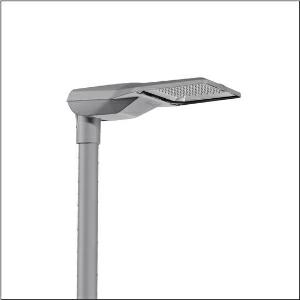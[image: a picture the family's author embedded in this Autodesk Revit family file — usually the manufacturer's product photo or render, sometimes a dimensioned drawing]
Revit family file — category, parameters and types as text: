
# Revit family: streetlight_sl_21_iq_midi___st0_8a_5xe3c31d08nb_f3e6
name_source: partatom
category: Lighting Fixtures
units: mm (PartAtom-declared; Revit-internal decimal feet)

## family parameters
Cut with Voids When Loaded = No
Host = Face
Light Source = No
Part Type = Normal
Room Calculation Point = No
Round Connector Dimension = Use Diameter
Shared = No

## types (1)
- --- (1 x LED, 23230 lm, 155.5 W, 3000K)
    Apparent Load = 155 VA
    CIE Flux Codes = 41 75 97 100 100
    Color Rendering = 70
    Color Temperature = 3000K
    Default Elevation = 1800 mm
    Description = Streetlight SL 21 iQ midi, mast luminaire, primary light control with lens, of PMMA, primary optical cover: cover, of toughened safety glass, transparent, light distribution: ST0.8a, light emission: direct distribution, primary light characteristic: asymmetric, installation type: post-top, side-entry, LED, High Power LED, rated luminous flux: 23.230lm, luminous efficacy: 149lm/W, light colour: 730, colour temperature: 3000K, control: Auto-Match, Temp-Guard, Lumen-Switch, Night-Set, Smart-Wire, Light-Fading, Desk-Remote (wireless, voltage-free reading and setting of iQ features in the workshop via application-optimized NFC function/RFID function), optimised constant luminous flux control (CLO 2.0), presetting dimming linear, mains connection: 230..240V, AC, 50/60Hz, start of lifetime: 156W, end of service life: 162W, reduction: 69W, luminaire housing, of diecast aluminium, powder-coated, Siteco® metallic grey (DB 702S), corrosivity category C5 mid according to DIN EN ISO 12944, please order mast flange separately, inclination adjustable: 0°, 5°, 10°, 15°, sealing non-destructively replaceable, multi-level sealing system, length: 644mm, width: 335mm, height: 110mm, mast flange for spigot size: 42mm (side-entry): 5XC10008XM4, 60/48mm (side-entry/post-top): 5XC10108XM2, 76/60mm (side-entry/post-top): 5XC10108XM1, protection rating (complete): IP66, insulation class (complete): insulation class II (safety insulation), certification: CE, ENEC, ENEC+, VDE, impact resistance: IK09, permissible operating ambient temperature for outdoor applications: -40..+50°C, standard-compliant lighting for roads and squares, packaging unit: 1 piece

Light Distribution: ST0.8a
    Height = 111 mm
    Lamp = 1 x LED
    Lamp Light Flux = 23230 lm
    Lamp Power = 155.5 W
    Lamp count = 1
    Length = 644 mm
    Luminous efficacy = 149 lm/W
    Manufacturer = Siteco
    ModVariant = No
    Model = 5XE3C31D08NB
    Number of Poles = 1
    OnlyDefault = Yes
    Power Factor = 1
    Product Name = Streetlight SL 21 iQ midi | ST0.8a
    Product group = mast luminaire | pylon top
    ProductGroupID = 6100
    Protection Class = Protection class II
    Protection Degree = IP 66
    RLX_Detail_Level = 1
    RLX_Emergency_Light_Flux = 0 lm
    RLX_Emergency_Type = 0
    RLX_Emergency_Type_DB = No
    RlxData = <blob elided: 91077 chars, md5=40db78cf>
    Socket = socket
    Standby Power = 0 W
    System Light Flux = 23230 lm
    System Power = 155 W
    Type Comments = factory setting: luminous flux: 100 % | dim-lin: 254 | 823 mA
    Type Image = l_1004298.jpg
    URL = http://relux.com
    VarID = @adj_119277
    Voltage = 0 V
    Weight = 0.00 kg
    Width = 336 mm

## geometry (parser evidence)
native form markers: Blend x4, Sweep x11
no freeform markers — native parametric forms only
